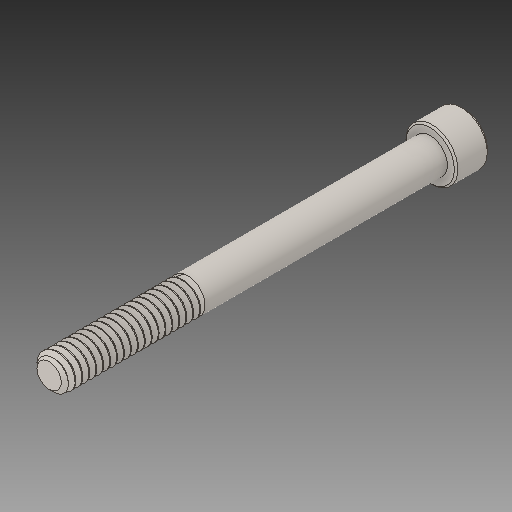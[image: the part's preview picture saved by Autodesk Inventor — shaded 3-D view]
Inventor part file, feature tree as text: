
AUTODESK INVENTOR PART (.ipt)
format: ipt  version: 2017 (Build 210142000, 142)  size: 644,096 bytes
history: native  units: in
note: dims shown in document units (in); Inventor stores cm internally (conversion verified against a paired STEP export)
features: chamfer x1
ambient origin geometry x8: Origin, YZ Plane, XZ Plane, XY Plane, X Axis, Y Axis, Z Axis, Center Point
bodies: Solid1 (feature_tree)
feature tree (1):
  chamfer  "Chamfer2"  [1 undecoded]
note: 1 required parameter value undecoded (feature->parameter linkage not recoverable at this tier; creation-order binding heuristic only, values carry confidence <= 0.55)
